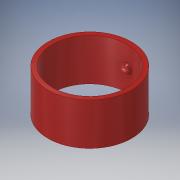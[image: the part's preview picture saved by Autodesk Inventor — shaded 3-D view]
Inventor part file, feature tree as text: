
AUTODESK INVENTOR PART (.ipt)
format: ipt  version: 2019.3 (Build 233278000, 278)  size: 121,856 bytes
history: native  units: in
note: dims shown in document units (in); Inventor stores cm internally (conversion verified against a paired STEP export)
features: sketch x2, extrude x1, revolve x1
ambient origin geometry x8: Origin, YZ Plane, XZ Plane, XY Plane, X Axis, Y Axis, Z Axis, Center Point
bodies: Solid1 (feature_tree)
feature tree (4):
  extrude  "Extrusion1"  Depth=1.99in
  revolve  "Revolution2"  [1 undecoded]
  sketch  "Sketch1"  dims[d0=1.78in d1=1.99in]
  sketch  "Sketch5"  dims[d2=1.0in d3=0.0in d6=0.0687in d7=0.115in]
note: 1 required parameter value undecoded (feature->parameter linkage not recoverable at this tier; creation-order binding heuristic only, values carry confidence <= 0.55)
